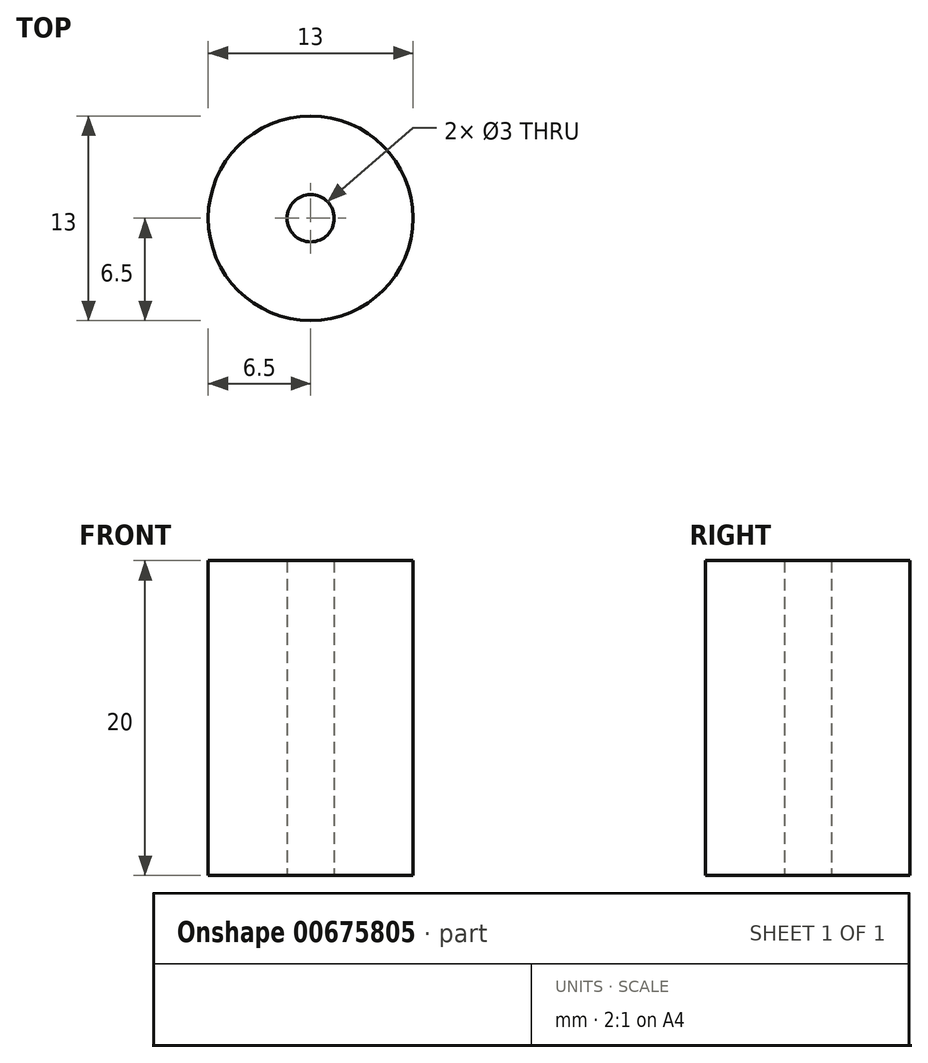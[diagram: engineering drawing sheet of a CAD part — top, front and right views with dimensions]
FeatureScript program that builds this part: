
annotation { "Feature Type Name" : "Feature", "Feature Type Description" : "" }
export const myFeature = defineFeature(function(context is Context, id is Id, definition is map)
    precondition{}
    {
        {
            var Q0;
            Q0=qCreatedBy(makeId("Front.planeOp"),FACE);
            var sketch = newSketch(context, id + "F0", { "sketchPlane" : qUnion([Q0])});
            skLineSegment(sketch, "E0", {"start": v(0, 0) * mm, "end": v(1.5, 0) * mm});
            skLineSegment(sketch, "E1", {"start": v(1.5, 0) * mm, "end": v(6.5, 0) * mm});
            skLineSegment(sketch, "E2", {"start": v(0, 0) * mm, "end": v(0, 20) * mm});
            skLineSegment(sketch, "E3", {"start": v(0, 20) * mm, "end": v(1.5, 20) * mm});
            skLineSegment(sketch, "E4", {"start": v(1.5, 20) * mm, "end": v(6.5, 20) * mm});
            skLineSegment(sketch, "E5", {"start": v(1.5, 20) * mm, "end": v(1.5, 0) * mm});
            skLineSegment(sketch, "E6", {"start": v(6.5, 20) * mm, "end": v(6.5, 0) * mm});
            skSolve(sketch);
        }
        {
            var Q0;
            Q0=makeQuery(id+"F0.imprint","IMPRINT",FACE,{"disambiguationData":[TD([[makeQuery(id+"F0.imprint","IMPRINT",EDGE,{"derivedFrom":sQuery(id+"F0.wireOp",EDGE,"E1")}),1.0]])]});
            var Q1;
            Q1=sQuery(id+"F0.wireOp",EDGE,"E2");
            revolve(context, id + "F1", {"entities" : qUnion([Q0]), "axis" : qUnion([Q1]), "revolveType" : RevolveType.FULL});
        }
    });
